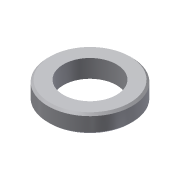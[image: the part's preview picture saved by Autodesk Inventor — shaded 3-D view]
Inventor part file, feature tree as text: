
AUTODESK INVENTOR PART (.ipt)
format: ipt  version: 2013 (Build 170138000, 138)  size: 79,360 bytes
history: native  units: in
note: dims shown in document units (in); Inventor stores cm internally (conversion verified against a paired STEP export)
features: chamfer x1, other x1, imported_body x1
ambient origin geometry x8: Origin, YZ Plane, XZ Plane, XY Plane, X Axis, Y Axis, Z Axis, Center Point
feature tree (3):
  chamfer  "Chamfer1"  [1 undecoded]
  other  "177x500 spacer_smart1"
  imported_body  "Base1"
note: 1 required parameter value undecoded (feature->parameter linkage not recoverable at this tier; creation-order binding heuristic only, values carry confidence <= 0.55)
